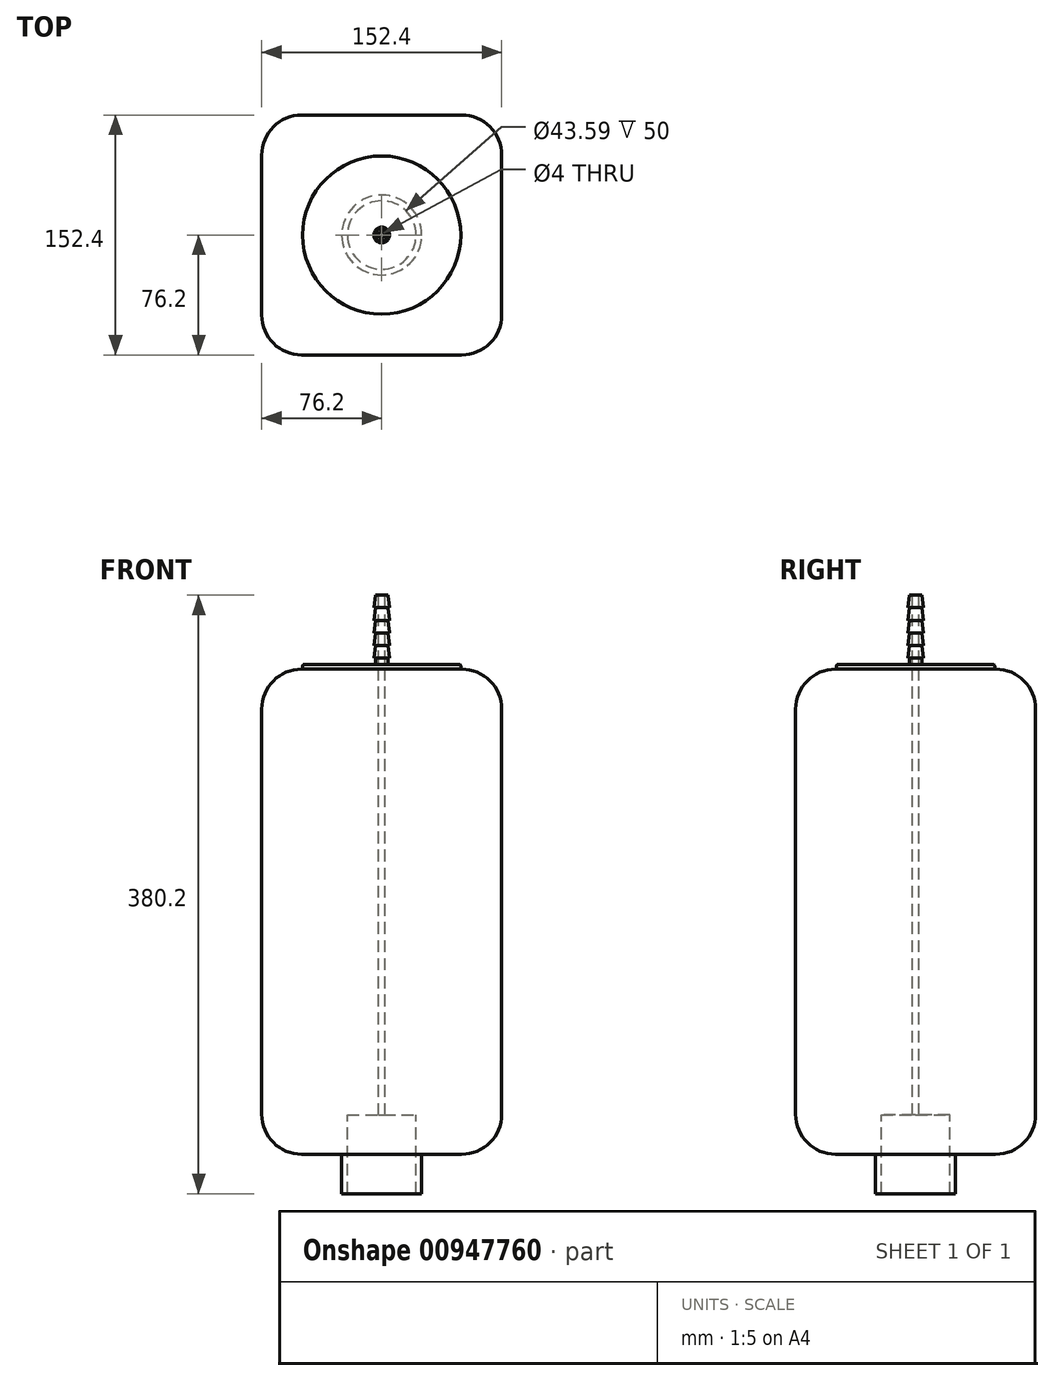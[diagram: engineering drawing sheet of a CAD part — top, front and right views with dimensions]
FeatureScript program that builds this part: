
annotation { "Feature Type Name" : "Feature", "Feature Type Description" : "" }
export const myFeature = defineFeature(function(context is Context, id is Id, definition is map)
    precondition{}
    {
        {
            var Q0;
            Q0=qCreatedBy(makeId("Top.planeOp"),FACE);
            var sketch = newSketch(context, id + "F0", { "sketchPlane" : qUnion([Q0])});
            skLineSegment(sketch, "E0.bottom", {"start": v(50.8, -76.2) * mm, "end": v(-50.8, -76.2) * mm});
            skLineSegment(sketch, "E0.top", {"start": v(50.8, 76.2) * mm, "end": v(-50.8, 76.2) * mm});
            skLineSegment(sketch, "E0.left", {"start": v(76.2, -50.8) * mm, "end": v(76.2, 50.8) * mm});
            skLineSegment(sketch, "E0.right", {"start": v(-76.2, -50.8) * mm, "end": v(-76.2, 50.8) * mm});
            skPoint(sketch, "E0.middle", {"position": v(0, 0) * mm});
            skPoint(sketch, "E1.visualSharp", {"position": v(-76.2, 76.2) * mm});
            skArc(sketch, "E1.filletArc", {"start": v(-50.8, 76.2) * mm, "mid": v(-68.76, 68.76) * mm, "end": v(-76.2, 50.8) * mm});
            skPoint(sketch, "E2.visualSharp", {"position": v(76.2, 76.2) * mm});
            skArc(sketch, "E2.filletArc", {"start": v(76.2, 50.8) * mm, "mid": v(68.76, 68.76) * mm, "end": v(50.8, 76.2) * mm});
            skPoint(sketch, "E3.visualSharp", {"position": v(76.2, -76.2) * mm});
            skArc(sketch, "E3.filletArc", {"start": v(50.8, -76.2) * mm, "mid": v(68.76, -68.76) * mm, "end": v(76.2, -50.8) * mm});
            skPoint(sketch, "E4.visualSharp", {"position": v(-76.2, -76.2) * mm});
            skArc(sketch, "E4.filletArc", {"start": v(-76.2, -50.8) * mm, "mid": v(-68.76, -68.76) * mm, "end": v(-50.8, -76.2) * mm});
            skSolve(sketch);
        }
        {
            var Q0;
            Q0 = qSketchRegion(id + "F0", true);
            extrude(context, id + "F1", {"entities" : qUnion([Q0]), "depth" : 308.2 * mm, "offsetDistance" : 25 * mm});
        }
        {
            var Q0;
            Q0=makeQuery(id+"F1.opExtrude","CAP_EDGE",EDGE,{"disambiguationData":[OSD([sQuery(id+"F0.wireOp",EDGE,"E0.bottom")])],"isStart":false});
            var Q1;
            Q1=makeQuery(id+"F1.opExtrude","CAP_EDGE",EDGE,{"disambiguationData":[OSD([sQuery(id+"F0.wireOp",EDGE,"E0.bottom")])],"isStart":true});
            fillet(context, id + "F2", {"entities" : qUnion([Q0, Q1]), "tangentPropagation" : true, "radius" : 25.4 * mm, "defaultsChanged" : false, "vertexSettings" : [], "allowEdgeOverflow" : false});
        }
        {
            var Q0;
            Q0=makeQuery(id+"F1.opExtrude","CAP_FACE",FACE,{"disambiguationData":[OSD([sQuery(id+"F0.wireOp",EDGE,"E0.bottom"),sQuery(id+"F0.wireOp",EDGE,"E0.top"),sQuery(id+"F0.wireOp",EDGE,"E0.left"),sQuery(id+"F0.wireOp",EDGE,"E0.right"),sQuery(id+"F0.wireOp",EDGE,"E1.filletArc"),sQuery(id+"F0.wireOp",EDGE,"E2.filletArc"),sQuery(id+"F0.wireOp",EDGE,"E3.filletArc"),sQuery(id+"F0.wireOp",EDGE,"E4.filletArc")])],"isStart":true});
            var sketch = newSketch(context, id + "F3", { "sketchPlane" : qUnion([Q0])});
            skCircle(sketch, "E5", {"center": v(0, 0) * mm, "radius": 21.8 * mm});
            skCircle(sketch, "E6", {"center": v(0, 0) * mm, "radius": 25.4 * mm});
            skSolve(sketch);
        }
        {
            var Q0;
            Q0 = qSketchRegion(id + "F3", true);
            extrude(context, id + "F4", {"entities" : qUnion([Q0]), "operationType" : NewBodyOperationType.ADD, "depth" : 25 * mm, "offsetDistance" : 25 * mm});
        }
        {
            var Q0;
            Q0=makeQuery(id+"F4.boolean.opBoolean","SPLIT",FACE,{"disambiguationData":[TD([makeQuery(id+"F4.opExtrude","SWEPT_FACE",FACE,{"disambiguationData":[OSD([sQuery(id+"F3.wireOp",EDGE,"E5")])]})])],"derivedFrom":makeQuery(id+"F1.opExtrude","CAP_FACE",FACE,{"disambiguationData":[OSD([sQuery(id+"F0.wireOp",EDGE,"E0.bottom"),sQuery(id+"F0.wireOp",EDGE,"E0.top"),sQuery(id+"F0.wireOp",EDGE,"E0.left"),sQuery(id+"F0.wireOp",EDGE,"E0.right"),sQuery(id+"F0.wireOp",EDGE,"E1.filletArc"),sQuery(id+"F0.wireOp",EDGE,"E2.filletArc"),sQuery(id+"F0.wireOp",EDGE,"E3.filletArc"),sQuery(id+"F0.wireOp",EDGE,"E4.filletArc")])],"isStart":true})});
            var sketch = newSketch(context, id + "F5", { "sketchPlane" : qUnion([Q0])});
            skCircle(sketch, "E7", {"center": v(0, 0) * mm, "radius": 21.8 * mm});
            skSolve(sketch);
        }
        {
            var Q0;
            Q0 = qSketchRegion(id + "F5", true);
            extrude(context, id + "F6", {"entities" : qUnion([Q0]), "operationType" : NewBodyOperationType.REMOVE, "oppositeDirection" : true, "depth" : 25 * mm, "offsetDistance" : 25 * mm});
        }
        {
            var Q0;
            Q0=qCreatedBy(makeId("Front.planeOp"),FACE);
            var sketch = newSketch(context, id + "F7", { "sketchPlane" : qUnion([Q0])});
            skLineSegment(sketch, "E8", {"start": v(0, 0) * mm, "end": v(0, 1062.87) * mm, "construction": true});
            skLineSegment(sketch, "E9", {"start": v(0, 308.2) * mm, "end": v(-50.21, 308.2) * mm});
            skLineSegment(sketch, "E10", {"start": v(-50.21, 308.2) * mm, "end": v(-50.21, 311.2) * mm});
            skLineSegment(sketch, "E11", {"start": v(-50.21, 311.2) * mm, "end": v(-4, 311.2) * mm});
            skLineSegment(sketch, "E12", {"start": v(-4, 311.2) * mm, "end": v(-4, 315.2) * mm});
            skLineSegment(sketch, "E13", {"start": v(-4, 315.2) * mm, "end": v(-5, 315.2) * mm});
            skLineSegment(sketch, "E14", {"start": v(-5, 315.2) * mm, "end": v(-4, 323.2) * mm});
            skLineSegment(sketch, "E15", {"start": v(-4, 323.2) * mm, "end": v(-5, 323.2) * mm});
            skLineSegment(sketch, "E16", {"start": v(-5, 323.2) * mm, "end": v(-4, 331.2) * mm});
            skLineSegment(sketch, "E17", {"start": v(-4, 331.2) * mm, "end": v(-5, 331.2) * mm});
            skLineSegment(sketch, "E18", {"start": v(-5, 331.2) * mm, "end": v(-4, 339.2) * mm});
            skLineSegment(sketch, "E19", {"start": v(-4, 339.2) * mm, "end": v(-5, 339.2) * mm});
            skLineSegment(sketch, "E20", {"start": v(-5, 339.2) * mm, "end": v(-4, 347.2) * mm});
            skLineSegment(sketch, "E21", {"start": v(-4, 347.2) * mm, "end": v(-5, 347.2) * mm});
            skLineSegment(sketch, "E22", {"start": v(-5, 347.2) * mm, "end": v(-4, 355.2) * mm});
            skLineSegment(sketch, "E23", {"start": v(-4, 355.2) * mm, "end": v(0, 355.2) * mm});
            skLineSegment(sketch, "E24", {"start": v(0, 355.2) * mm, "end": v(0, 308.2) * mm});
            skSolve(sketch);
        }
        {
            var Q0;
            Q0 = qSketchRegion(id + "F7", true);
            var Q1;
            Q1=sQuery(id+"F7.wireOp",EDGE,"E24");
            revolve(context, id + "F8", {"operationType" : NewBodyOperationType.ADD, "surfaceOperationType" : NewSurfaceOperationType.NEW, "entities" : qUnion([Q0]), "axis" : qUnion([Q1]), "revolveType" : RevolveType.FULL});
        }
        {
            var Q0;
            Q0=makeQuery(id+"F8.opRevolve","SWEPT_FACE",FACE,{"disambiguationData":[OSD([sQuery(id+"F7.wireOp",EDGE,"E23")])]});
            var sketch = newSketch(context, id + "F9", { "sketchPlane" : qUnion([Q0])});
            skPoint(sketch, "E25", {"position": v(0, 0) * mm});
            skCircle(sketch, "E26", {"center": v(0, 0) * mm, "radius": 2 * mm});
            skSolve(sketch);
        }
        {
            var Q0;
            Q0 = qSketchRegion(id + "F9", true);
            extrude(context, id + "F10", {"entities" : qUnion([Q0]), "operationType" : NewBodyOperationType.REMOVE, "endBound" : BoundingType.THROUGH_ALL, "oppositeDirection" : true, "depth" : 25 * mm, "offsetDistance" : 25 * mm});
        }
        {
            var Q0;
            Q0=makeQuery(id+"F8.opRevolve","SWEPT_EDGE",EDGE,{"disambiguationData":[OSD([sQuery(id+"F7.wireOp",EDGE,"E10"),sQuery(id+"F7.wireOp",EDGE,"E11")])]});
            fillet(context, id + "F11", {"entities" : qUnion([Q0]), "tangentPropagation" : true, "radius" : 1 * mm, "defaultsChanged" : false, "vertexSettings" : [], "allowEdgeOverflow" : false});
        }
    });
